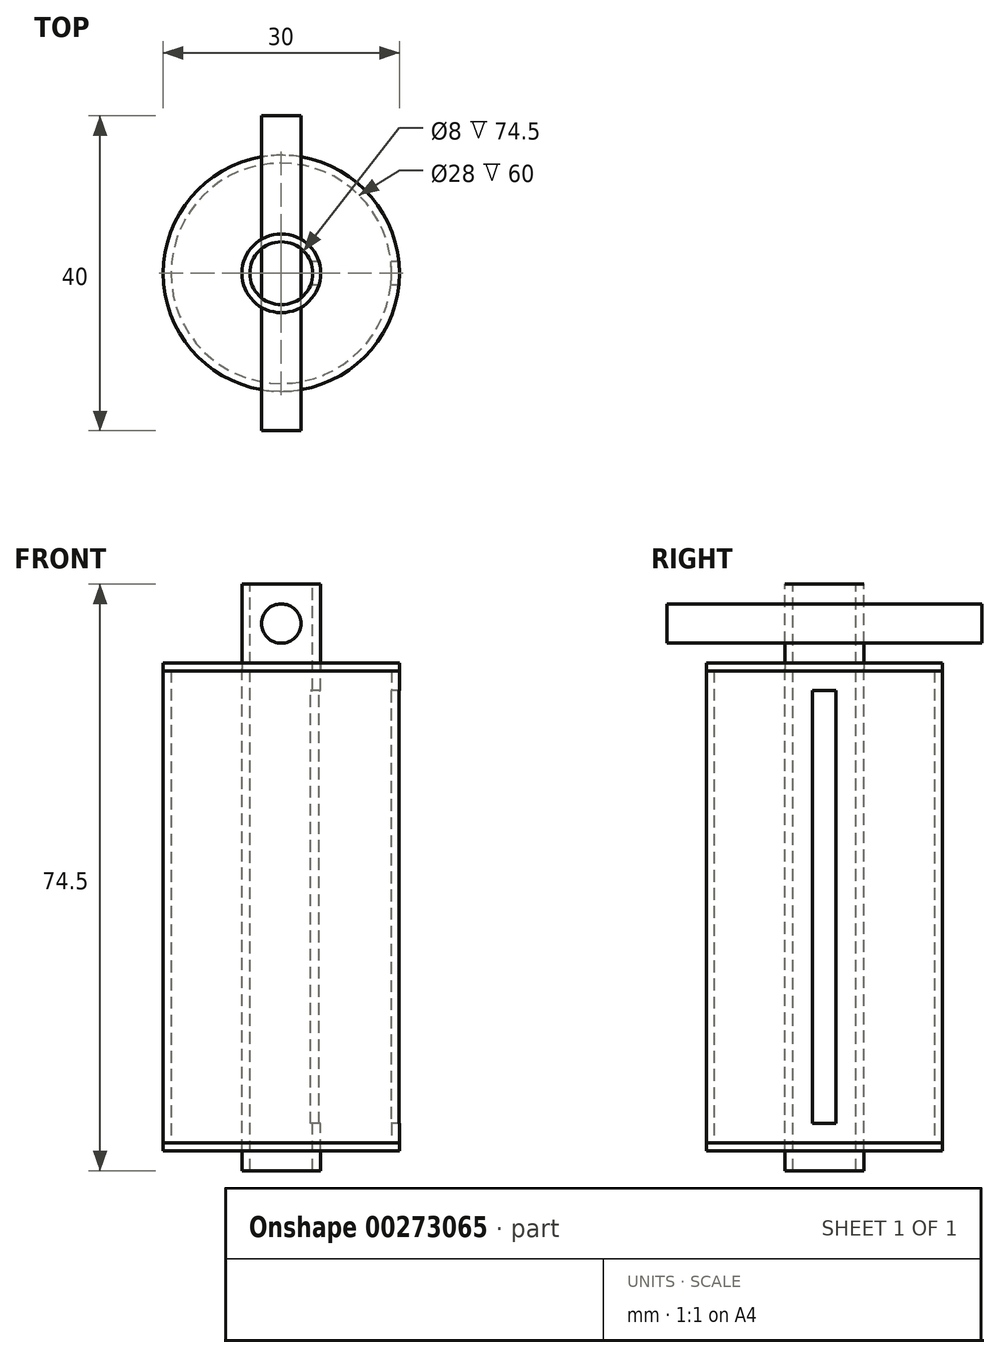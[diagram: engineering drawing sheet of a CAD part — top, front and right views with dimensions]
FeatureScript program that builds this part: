
annotation { "Feature Type Name" : "Feature", "Feature Type Description" : "" }
export const myFeature = defineFeature(function(context is Context, id is Id, definition is map)
    precondition{}
    {
        {
            var Q0;
            Q0=qCreatedBy(makeId("Top.planeOp"),FACE);
            var sketch = newSketch(context, id + "F0", { "sketchPlane" : qUnion([Q0])});
            skCircle(sketch, "E0", {"center": v(0, 0) * mm, "radius": 14 * mm});
            skCircle(sketch, "E1", {"center": v(0, 0) * mm, "radius": 15 * mm});
            skSolve(sketch);
        }
        {
            var Q0;
            Q0 = qSketchRegion(id + "F0", true);
            extrude(context, id + "F1", {"entities" : qUnion([Q0]), "endBound" : BoundingType.SYMMETRIC, "depth" : 60 * mm});
        }
        {
            var Q0;
            Q0=makeQuery(id+"F1.opExtrude","CAP_FACE",FACE,{"disambiguationData":[OSD([sQuery(id+"F0.wireOp",EDGE,"E0"),sQuery(id+"F0.wireOp",EDGE,"E1")])],"isStart":false});
            var sketch = newSketch(context, id + "F2", { "sketchPlane" : qUnion([Q0])});
            skCircle(sketch, "E2.0", {"center": v(0, 0) * mm, "radius": 15 * mm});
            skCircle(sketch, "E3", {"center": v(0, 0) * mm, "radius": 5 * mm});
            skSolve(sketch);
        }
        {
            var Q0;
            Q0 = qSketchRegion(id + "F2", true);
            extrude(context, id + "F3", {"entities" : qUnion([Q0]), "depth" : 1 * mm});
        }
        {
            var Q0;
            Q0=makeQuery(id+"F3.opExtrude","SWEPT_BODY",BODY,{"disambiguationData":[OSD([sQuery(id+"F2.wireOp",EDGE,"E2.0"),sQuery(id+"F2.wireOp",EDGE,"E3")])]});
            var Q1;
            Q1=qCreatedBy(makeId("Top.planeOp"),FACE);
            mirror(context, id + "F4", {"entities" : qUnion([Q0]), "mirrorPlane" : qUnion([Q1])});
        }
        {
            var Q0;
            Q0=makeQuery(id+"F3.opExtrude","CAP_FACE",FACE,{"disambiguationData":[OSD([sQuery(id+"F2.wireOp",EDGE,"E2.0"),sQuery(id+"F2.wireOp",EDGE,"E3")])],"isStart":false});
            var sketch = newSketch(context, id + "F5", { "sketchPlane" : qUnion([Q0])});
            skCircle(sketch, "E4.0", {"center": v(0, 0) * mm, "radius": 5 * mm});
            skCircle(sketch, "E5", {"center": v(0, 0) * mm, "radius": 4 * mm});
            skSolve(sketch);
        }
        {
            var Q0;
            Q0 = qSketchRegion(id + "F5", true);
            extrude(context, id + "F6", {"entities" : qUnion([Q0]), "oppositeDirection" : true, "depth" : 64.5 * mm, "hasSecondDirection" : true, "secondDirectionOppositeDirection" : false, "secondDirectionDepth" : 10 * mm});
        }
        {
            var Q0;
            Q0=qCreatedBy(makeId("Right.planeOp"),FACE);
            var sketch = newSketch(context, id + "F7", { "sketchPlane" : qUnion([Q0])});
            skLineSegment(sketch, "E6.bottom", {"start": v(-1.5, -27.5) * mm, "end": v(1.5, -27.5) * mm});
            skLineSegment(sketch, "E6.top", {"start": v(-1.5, 27.5) * mm, "end": v(1.5, 27.5) * mm});
            skLineSegment(sketch, "E6.left", {"start": v(-1.5, -27.5) * mm, "end": v(-1.5, 27.5) * mm});
            skLineSegment(sketch, "E6.right", {"start": v(1.5, -27.5) * mm, "end": v(1.5, 27.5) * mm});
            skPoint(sketch, "E6.middle", {"position": v(0, 0) * mm});
            skSolve(sketch);
        }
        {
            var Q0;
            Q0 = qSketchRegion(id + "F7", true);
            extrude(context, id + "F8", {"entities" : qUnion([Q0]), "operationType" : NewBodyOperationType.REMOVE, "depth" : 25 * mm});
        }
        {
            var Q0;
            Q0=qCreatedBy(makeId("Front.planeOp"),FACE);
            var sketch = newSketch(context, id + "F9", { "sketchPlane" : qUnion([Q0])});
            skCircle(sketch, "E7", {"center": v(0, 36) * mm, "radius": 2.5 * mm});
            skSolve(sketch);
        }
        {
            var Q0;
            Q0 = qSketchRegion(id + "F9", true);
            extrude(context, id + "F10", {"entities" : qUnion([Q0]), "endBound" : BoundingType.SYMMETRIC, "depth" : 40 * mm});
        }
    });
